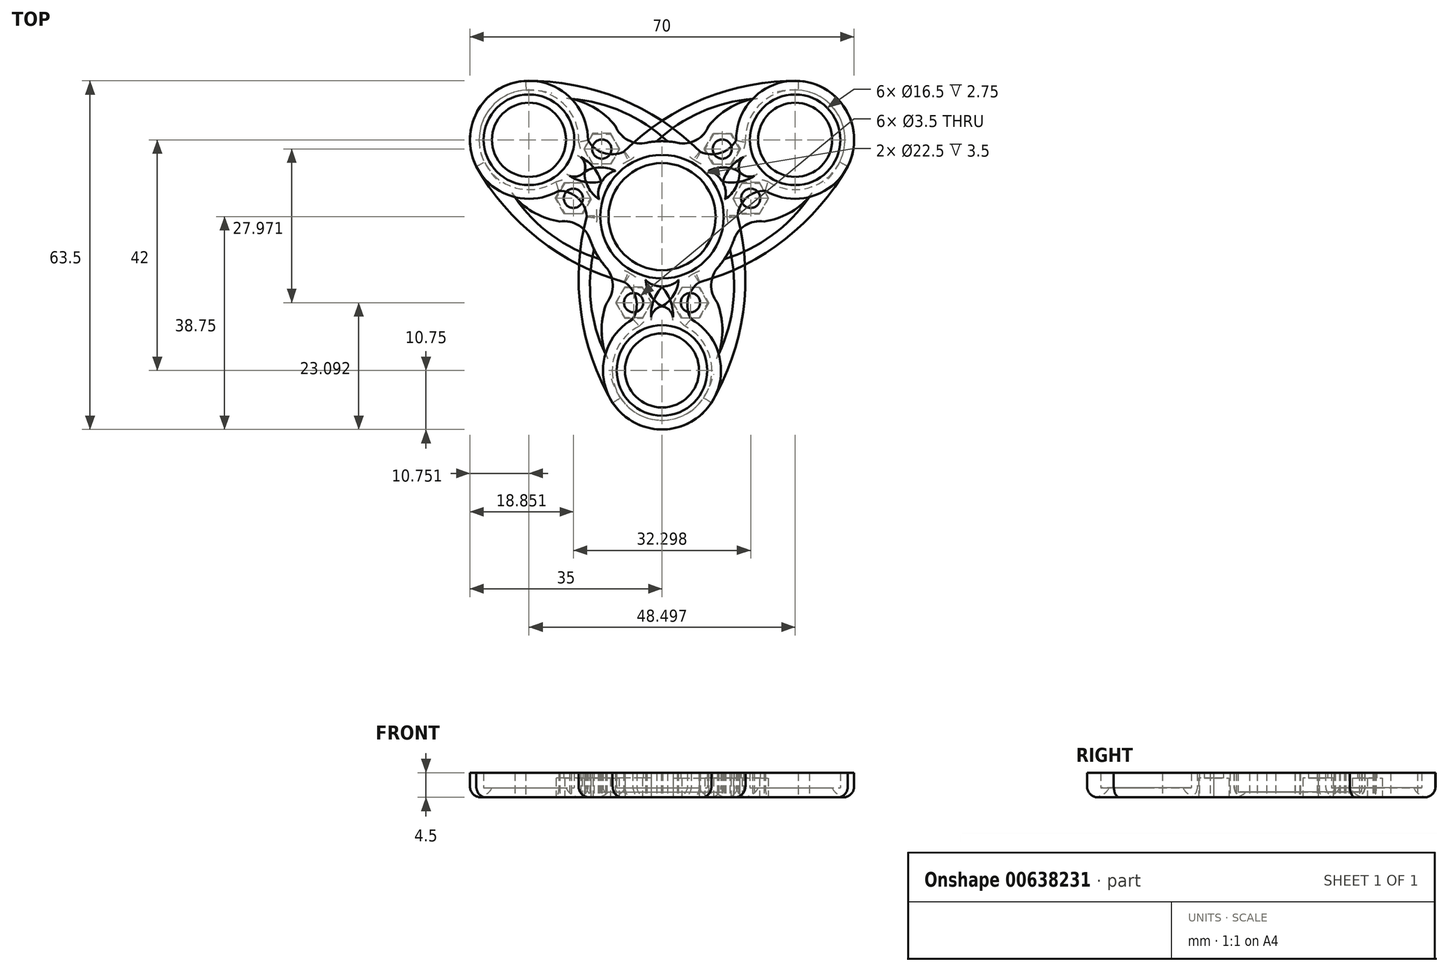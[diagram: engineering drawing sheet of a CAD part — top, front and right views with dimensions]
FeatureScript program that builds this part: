
annotation { "Feature Type Name" : "Feature", "Feature Type Description" : "" }
export const myFeature = defineFeature(function(context is Context, id is Id, definition is map)
    precondition{}
    {
        {
            assignVariable(context, id + "F0", {"name" : "OuterBearingHeight", "anyValue" : 5});
        }
        {
            assignVariable(context, id + "F1", {"name" : "CenterBearingHeight", "anyValue" : 7});
        }
        {
            var Q0;
            Q0=qCreatedBy(makeId("Top.planeOp"),FACE);
            var sketch = newSketch(context, id + "F2", { "sketchPlane" : qUnion([Q0])});
            skCircle(sketch, "E0", {"center": v(0, 0) * mm, "radius": 11.25 * mm});
            skCircle(sketch, "E1", {"center": v(0, 0) * mm, "radius": 9.75 * mm});
            skCircle(sketch, "E2", {"center": v(0, 0) * mm, "radius": 13.75 * mm});
            skCircle(sketch, "E3", {"center": v(0, -28) * mm, "radius": 10.75 * mm});
            skArc(sketch, "E4", {"start": v(-13.75, 0) * mm, "mid": v(-14.77, -17.41) * mm, "end": v(-9, -33.88) * mm});
            skArc(sketch, "E5", {"start": v(6.75, -11.98) * mm, "mid": v(4.65, -16.78) * mm, "end": v(8, -20.82) * mm});
            skPoint(sketch, "E6.center", {"position": v(0.04, 0.07) * mm});
            skCircle(sketch, "E7.cCircle", {"center": v(-5.18, -15.66) * mm, "radius": 2.75 * mm, "construction": true});
            skLineSegment(sketch, "E7.0", {"start": v(-3.59, -18.4) * mm, "end": v(-6.76, -18.4) * mm});
            skLineSegment(sketch, "E7.1", {"start": v(-6.76, -18.4) * mm, "end": v(-8.35, -15.66) * mm});
            skLineSegment(sketch, "E7.2", {"start": v(-8.35, -15.66) * mm, "end": v(-6.76, -12.9) * mm});
            skLineSegment(sketch, "E7.3", {"start": v(-6.76, -12.9) * mm, "end": v(-3.59, -12.9) * mm});
            skLineSegment(sketch, "E7.4", {"start": v(-3.59, -12.9) * mm, "end": v(-2, -15.66) * mm});
            skLineSegment(sketch, "E7.5", {"start": v(-2, -15.66) * mm, "end": v(-3.59, -18.4) * mm});
            skPoint(sketch, "E7.0.midPoint", {"position": v(-5.18, -18.4) * mm});
            skLineSegment(sketch, "E8", {"start": v(-5.18, -15.66) * mm, "end": v(-5.18, -12.74) * mm, "construction": true});
            skLineSegment(sketch, "E9", {"start": v(-5.18, -15.66) * mm, "end": v(-5.18, -18.58) * mm, "construction": true});
            skLineSegment(sketch, "E10", {"start": v(-5.18, -15.66) * mm, "end": v(-14.98, -15.66) * mm, "construction": true});
            skLineSegment(sketch, "E11", {"start": v(-5.18, -15.66) * mm, "end": v(4.62, -15.66) * mm, "construction": true});
            skCircle(sketch, "E12", {"center": v(-5.18, -15.66) * mm, "radius": 1.75 * mm});
            skArc(sketch, "E13", {"start": v(-12.37, -6) * mm, "mid": v(-12.96, -15.68) * mm, "end": v(-10.33, -25.02) * mm});
            skArc(sketch, "E14", {"start": v(-10.08, -15.66) * mm, "mid": v(-11, -20.32) * mm, "end": v(-10.33, -25.02) * mm});
            skArc(sketch, "E15", {"start": v(-10.08, -15.66) * mm, "mid": v(-8.97, -12.35) * mm, "end": v(-10.29, -9.12) * mm});
            skArc(sketch, "E16", {"start": v(2, -18.27) * mm, "mid": v(0.72, -13.72) * mm, "end": v(-3.01, -10.84) * mm});
            skArc(sketch, "E17", {"start": v(2, -18.27) * mm, "mid": v(1.3, -16.98) * mm, "end": v(0, -16.32) * mm});
            skArc(sketch, "E18", {"start": v(-3.01, -10.84) * mm, "mid": v(-2.27, -14) * mm, "end": v(0, -16.32) * mm});
            skCircle(sketch, "E19", {"center": v(0, -28) * mm, "radius": 8.25 * mm});
            skCircle(sketch, "E20", {"center": v(0, -28) * mm, "radius": 6.75 * mm});
            skArc(sketch, "E21", {"start": v(-3, -11.56) * mm, "mid": v(-1.67, -12.41) * mm, "end": v(-0.12, -12.69) * mm});
            skArc(sketch, "E22.1.0", {"start": v(6.87, -11.9) * mm, "mid": v(22.46, -4.08) * mm, "end": v(33.84, 9.15) * mm});
            skArc(sketch, "E22.1.1", {"start": v(11.38, -7.71) * mm, "mid": v(20.06, -3.39) * mm, "end": v(26.83, 3.56) * mm});
            skArc(sketch, "E22.1.2", {"start": v(18.6, -0.9) * mm, "mid": v(15.18, -1.59) * mm, "end": v(13.04, -4.35) * mm});
            skArc(sketch, "E22.1.3", {"start": v(18.6, -0.9) * mm, "mid": v(23.1, 0.63) * mm, "end": v(26.83, 3.56) * mm});
            skLineSegment(sketch, "E22.1.4", {"start": v(19.32, 3.35) * mm, "end": v(17.74, 0.6) * mm});
            skLineSegment(sketch, "E22.1.5", {"start": v(17.74, 0.6) * mm, "end": v(14.56, 0.6) * mm});
            skLineSegment(sketch, "E22.1.6", {"start": v(14.56, 0.6) * mm, "end": v(12.97, 3.35) * mm});
            skLineSegment(sketch, "E22.1.7", {"start": v(12.97, 3.35) * mm, "end": v(14.56, 6.1) * mm});
            skLineSegment(sketch, "E22.1.8", {"start": v(14.56, 6.1) * mm, "end": v(17.74, 6.1) * mm});
            skLineSegment(sketch, "E22.1.9", {"start": v(17.74, 6.1) * mm, "end": v(19.32, 3.35) * mm});
            skCircle(sketch, "E22.1.10", {"center": v(24.25, 14) * mm, "radius": 10.75 * mm});
            skCircle(sketch, "E22.1.11", {"center": v(24.25, 14) * mm, "radius": 8.25 * mm});
            skCircle(sketch, "E22.1.12", {"center": v(24.25, 14) * mm, "radius": 6.75 * mm});
            skArc(sketch, "E22.1.13", {"start": v(10.9, 2.81) * mm, "mid": v(13.26, 5.03) * mm, "end": v(14.13, 8.16) * mm});
            skArc(sketch, "E22.1.14", {"start": v(14.82, 10.86) * mm, "mid": v(11.52, 7.49) * mm, "end": v(10.9, 2.81) * mm});
            skArc(sketch, "E22.1.15", {"start": v(7, 11.84) * mm, "mid": v(12.2, 12.42) * mm, "end": v(14.03, 17.34) * mm});
            skArc(sketch, "E22.1.16", {"start": v(14.82, 10.86) * mm, "mid": v(14.06, 9.62) * mm, "end": v(14.13, 8.16) * mm});
            skArc(sketch, "E22.1.17", {"start": v(11.5, 3.18) * mm, "mid": v(11.59, 4.76) * mm, "end": v(11.05, 6.24) * mm});
            skCircle(sketch, "E22.1.18", {"center": v(16.15, 3.35) * mm, "radius": 1.75 * mm});
            skArc(sketch, "E22.2.0", {"start": v(6.87, 11.9) * mm, "mid": v(-7.7, 21.5) * mm, "end": v(-24.84, 24.73) * mm});
            skArc(sketch, "E22.2.1", {"start": v(1, 13.71) * mm, "mid": v(-7.1, 19.07) * mm, "end": v(-16.5, 21.45) * mm});
            skArc(sketch, "E22.2.2", {"start": v(-8.52, 16.56) * mm, "mid": v(-6.21, 13.94) * mm, "end": v(-2.75, 13.47) * mm});
            skArc(sketch, "E22.2.3", {"start": v(-8.52, 16.56) * mm, "mid": v(-12.1, 19.7) * mm, "end": v(-16.5, 21.45) * mm});
            skLineSegment(sketch, "E22.2.4", {"start": v(-12.56, 15.06) * mm, "end": v(-9.38, 15.06) * mm});
            skLineSegment(sketch, "E22.2.5", {"start": v(-9.38, 15.06) * mm, "end": v(-7.8, 12.31) * mm});
            skLineSegment(sketch, "E22.2.6", {"start": v(-7.8, 12.31) * mm, "end": v(-9.38, 9.56) * mm});
            skLineSegment(sketch, "E22.2.7", {"start": v(-9.38, 9.56) * mm, "end": v(-12.56, 9.56) * mm});
            skLineSegment(sketch, "E22.2.8", {"start": v(-12.56, 9.56) * mm, "end": v(-14.15, 12.31) * mm});
            skLineSegment(sketch, "E22.2.9", {"start": v(-14.15, 12.31) * mm, "end": v(-12.56, 15.06) * mm});
            skCircle(sketch, "E22.2.10", {"center": v(-24.25, 14) * mm, "radius": 10.75 * mm});
            skCircle(sketch, "E22.2.11", {"center": v(-24.25, 14) * mm, "radius": 8.25 * mm});
            skCircle(sketch, "E22.2.12", {"center": v(-24.25, 14) * mm, "radius": 6.75 * mm});
            skArc(sketch, "E22.2.13", {"start": v(-7.88, 8.03) * mm, "mid": v(-10.99, 8.97) * mm, "end": v(-14.13, 8.16) * mm});
            skArc(sketch, "E22.2.14", {"start": v(-16.82, 7.4) * mm, "mid": v(-12.25, 6.24) * mm, "end": v(-7.88, 8.03) * mm});
            skArc(sketch, "E22.2.15", {"start": v(-13.75, 0.14) * mm, "mid": v(-16.86, 4.36) * mm, "end": v(-22.03, 3.48) * mm});
            skArc(sketch, "E22.2.16", {"start": v(-16.82, 7.4) * mm, "mid": v(-15.36, 7.37) * mm, "end": v(-14.13, 8.16) * mm});
            skArc(sketch, "E22.2.17", {"start": v(-8.5, 8.38) * mm, "mid": v(-9.91, 7.66) * mm, "end": v(-10.93, 6.45) * mm});
            skCircle(sketch, "E22.2.18", {"center": v(-10.97, 12.31) * mm, "radius": 1.75 * mm});
            skSolve(sketch);
        }
        {
            var Q0;
            {var subQ0=sQuery(id+"F2.wireOp",EDGE,"E22.2.15");var subQ1=sQuery(id+"F2.wireOp",EDGE,"E2");var subQ2=makeQuery(id+"F2.imprint","INTERSECT",VERTEX,{"derivedFrom":[subQ1,subQ0]});Q0=makeQuery(id+"F2.imprint","IMPRINT",FACE,{"disambiguationData":[TD([[makeQuery(id+"F2.imprint","IMPRINT",EDGE,{"disambiguationData":[TD([[subQ2,1.0]])],"derivedFrom":subQ1}),-1.0]])]});}
            var Q1;
            {var subQ5=sQuery(id+"F2.wireOp",EDGE,"E22.2.7");var subQ7=sQuery(id+"F2.wireOp",EDGE,"E2");var subQ8=makeQuery(id+"F2.imprint","INTERSECT",VERTEX,{"derivedFrom":[subQ7,subQ5]});Q1=makeQuery(id+"F2.imprint","IMPRINT",FACE,{"disambiguationData":[TD([[makeQuery(id+"F2.imprint","IMPRINT",EDGE,{"disambiguationData":[TD([[subQ8,-1.0]])],"derivedFrom":subQ7}),-1.0]])]});}
            var Q2;
            {var subQ1=sQuery(id+"F2.wireOp",EDGE,"E22.2.3");Q2=makeQuery(id+"F2.imprint","IMPRINT",FACE,{"disambiguationData":[TD([[makeQuery(id+"F2.imprint","IMPRINT",EDGE,{"derivedFrom":subQ1}),1.0]])]});}
            var Q3;
            {var subQ3=sQuery(id+"F2.wireOp",EDGE,"E22.2.1");Q3=makeQuery(id+"F2.imprint","IMPRINT",FACE,{"disambiguationData":[TD([[makeQuery(id+"F2.imprint","IMPRINT",EDGE,{"derivedFrom":subQ3}),-1.0]])]});}
            var Q4;
            {var subQ3=sQuery(id+"F2.wireOp",EDGE,"E13");Q4=makeQuery(id+"F2.imprint","IMPRINT",FACE,{"disambiguationData":[TD([[makeQuery(id+"F2.imprint","IMPRINT",EDGE,{"derivedFrom":subQ3}),-1.0]])]});}
            var Q5;
            {var subQ0=sQuery(id+"F2.wireOp",EDGE,"E7.1");Q5=makeQuery(id+"F2.imprint","IMPRINT",FACE,{"disambiguationData":[TD([[makeQuery(id+"F2.imprint","IMPRINT",EDGE,{"derivedFrom":subQ0}),1.0]])]});}
            var Q6;
            {var subQ1=sQuery(id+"F2.wireOp",EDGE,"E7.4");var subQ5=sQuery(id+"F2.wireOp",EDGE,"E2");var subQ6=makeQuery(id+"F2.imprint","INTERSECT",VERTEX,{"derivedFrom":[subQ5,subQ1]});Q6=makeQuery(id+"F2.imprint","IMPRINT",FACE,{"disambiguationData":[TD([[makeQuery(id+"F2.imprint","IMPRINT",EDGE,{"disambiguationData":[TD([[subQ6,-1.0]])],"derivedFrom":subQ5}),-1.0]])]});}
            var Q7;
            {var subQ0=sQuery(id+"F2.wireOp",EDGE,"E5");var subQ1=sQuery(id+"F2.wireOp",EDGE,"E2");var subQ2=makeQuery(id+"F2.imprint","INTERSECT",VERTEX,{"derivedFrom":[subQ1,subQ0]});Q7=makeQuery(id+"F2.imprint","IMPRINT",FACE,{"disambiguationData":[TD([[makeQuery(id+"F2.imprint","IMPRINT",EDGE,{"disambiguationData":[TD([[subQ2,1.0]])],"derivedFrom":subQ1}),-1.0]])]});}
            var Q8;
            {var subQ3=sQuery(id+"F2.wireOp",EDGE,"E22.1.1");Q8=makeQuery(id+"F2.imprint","IMPRINT",FACE,{"disambiguationData":[TD([[makeQuery(id+"F2.imprint","IMPRINT",EDGE,{"derivedFrom":subQ3}),-1.0]])]});}
            var Q9;
            {var subQ1=sQuery(id+"F2.wireOp",EDGE,"E22.1.3");Q9=makeQuery(id+"F2.imprint","IMPRINT",FACE,{"disambiguationData":[TD([[makeQuery(id+"F2.imprint","IMPRINT",EDGE,{"derivedFrom":subQ1}),1.0]])]});}
            var Q10;
            {var subQ5=sQuery(id+"F2.wireOp",EDGE,"E22.1.7");var subQ7=sQuery(id+"F2.wireOp",EDGE,"E2");var subQ8=makeQuery(id+"F2.imprint","INTERSECT",VERTEX,{"derivedFrom":[subQ7,subQ5]});Q10=makeQuery(id+"F2.imprint","IMPRINT",FACE,{"disambiguationData":[TD([[makeQuery(id+"F2.imprint","IMPRINT",EDGE,{"disambiguationData":[TD([[subQ8,-1.0]])],"derivedFrom":subQ7}),-1.0]])]});}
            var Q11;
            {var subQ0=sQuery(id+"F2.wireOp",EDGE,"E22.1.15");var subQ1=sQuery(id+"F2.wireOp",EDGE,"E2");var subQ2=makeQuery(id+"F2.imprint","INTERSECT",VERTEX,{"derivedFrom":[subQ1,subQ0]});Q11=makeQuery(id+"F2.imprint","IMPRINT",FACE,{"disambiguationData":[TD([[makeQuery(id+"F2.imprint","IMPRINT",EDGE,{"disambiguationData":[TD([[subQ2,1.0]])],"derivedFrom":subQ1}),-1.0]])]});}
            var Q12;
            Q12=makeQuery(id+"F2.imprint","IMPRINT",FACE,{"disambiguationData":[TD([[makeQuery(id+"F2.imprint","IMPRINT",EDGE,{"derivedFrom":sQuery(id+"F2.wireOp",EDGE,"E22.2.11")}),-1.0]])]});
            var Q13;
            Q13=makeQuery(id+"F2.imprint","IMPRINT",FACE,{"disambiguationData":[TD([[makeQuery(id+"F2.imprint","IMPRINT",EDGE,{"derivedFrom":sQuery(id+"F2.wireOp",EDGE,"E22.1.11")}),-1.0]])]});
            var Q14;
            Q14=makeQuery(id+"F2.imprint","IMPRINT",FACE,{"disambiguationData":[TD([[makeQuery(id+"F2.imprint","IMPRINT",EDGE,{"derivedFrom":sQuery(id+"F2.wireOp",EDGE,"E19")}),-1.0]])]});
            var Q15;
            {var subQ0=sQuery(id+"F2.wireOp",EDGE,"E5");var subQ1=sQuery(id+"F2.wireOp",EDGE,"E3");var subQ2=makeQuery(id+"F2.imprint","INTERSECT",VERTEX,{"disambiguationData":[OD(0.0)],"derivedFrom":[subQ1,subQ0]});Q15=makeQuery(id+"F2.imprint","IMPRINT",FACE,{"disambiguationData":[TD([[makeQuery(id+"F2.imprint","IMPRINT",EDGE,{"disambiguationData":[TD([[subQ2,-1.0]])],"derivedFrom":subQ1}),1.0]])]});}
            var Q16;
            {var subQ0=sQuery(id+"F2.wireOp",EDGE,"E22.1.15");var subQ1=sQuery(id+"F2.wireOp",EDGE,"E22.1.10");var subQ2=makeQuery(id+"F2.imprint","INTERSECT",VERTEX,{"disambiguationData":[OD(0.0)],"derivedFrom":[subQ1,subQ0]});Q16=makeQuery(id+"F2.imprint","IMPRINT",FACE,{"disambiguationData":[TD([[makeQuery(id+"F2.imprint","IMPRINT",EDGE,{"disambiguationData":[TD([[subQ2,-1.0]])],"derivedFrom":subQ1}),1.0]])]});}
            var Q17;
            {var subQ0=sQuery(id+"F2.wireOp",EDGE,"E22.2.15");var subQ1=sQuery(id+"F2.wireOp",EDGE,"E22.2.10");var subQ2=makeQuery(id+"F2.imprint","INTERSECT",VERTEX,{"disambiguationData":[OD(0.0)],"derivedFrom":[subQ1,subQ0]});Q17=makeQuery(id+"F2.imprint","IMPRINT",FACE,{"disambiguationData":[TD([[makeQuery(id+"F2.imprint","IMPRINT",EDGE,{"disambiguationData":[TD([[subQ2,-1.0]])],"derivedFrom":subQ1}),1.0]])]});}
            var Q18;
            {var subQ1=sQuery(id+"F2.wireOp",EDGE,"E2");var subQ17=makeQuery(id+"F2.imprint","INTERSECT",VERTEX,{"derivedFrom":[subQ1,sQuery(id+"F2.wireOp",EDGE,"E22.2.15")]});Q18=makeQuery(id+"F2.imprint","IMPRINT",FACE,{"disambiguationData":[TD([[makeQuery(id+"F2.imprint","IMPRINT",EDGE,{"disambiguationData":[TD([[subQ17,1.0]])],"derivedFrom":subQ1}),1.0]])]});}
            var Q19;
            {var subQ4=sQuery(id+"F2.wireOp",EDGE,"E2");var subQ16=makeQuery(id+"F2.imprint","INTERSECT",VERTEX,{"derivedFrom":[subQ4,sQuery(id+"F2.wireOp",EDGE,"E22.1.15")]});Q19=makeQuery(id+"F2.imprint","IMPRINT",FACE,{"disambiguationData":[TD([[makeQuery(id+"F2.imprint","IMPRINT",EDGE,{"disambiguationData":[TD([[subQ16,1.0]])],"derivedFrom":subQ4}),1.0]])]});}
            var Q20;
            {var subQ1=sQuery(id+"F2.wireOp",EDGE,"E2");var subQ15=sQuery(id+"F2.wireOp",EDGE,"E22.1.7");var subQ16=makeQuery(id+"F2.imprint","INTERSECT",VERTEX,{"derivedFrom":[subQ1,subQ15]});Q20=makeQuery(id+"F2.imprint","IMPRINT",FACE,{"disambiguationData":[TD([[makeQuery(id+"F2.imprint","IMPRINT",EDGE,{"disambiguationData":[TD([[subQ16,-1.0]])],"derivedFrom":subQ1}),1.0]])]});}
            var Q21;
            {var subQ5=sQuery(id+"F2.wireOp",EDGE,"E22.2.17");Q21=makeQuery(id+"F2.imprint","IMPRINT",FACE,{"disambiguationData":[TD([[makeQuery(id+"F2.imprint","IMPRINT",EDGE,{"derivedFrom":subQ5}),1.0]])]});}
            var Q22;
            {var subQ5=sQuery(id+"F2.wireOp",EDGE,"E22.1.17");Q22=makeQuery(id+"F2.imprint","IMPRINT",FACE,{"disambiguationData":[TD([[makeQuery(id+"F2.imprint","IMPRINT",EDGE,{"derivedFrom":subQ5}),1.0]])]});}
            var Q23;
            {var subQ5=sQuery(id+"F2.wireOp",EDGE,"E21");Q23=makeQuery(id+"F2.imprint","IMPRINT",FACE,{"disambiguationData":[TD([[makeQuery(id+"F2.imprint","IMPRINT",EDGE,{"derivedFrom":subQ5}),1.0]])]});}
            extrude(context, id + "F3", {"entities" : qUnion([Q0, Q1, Q2, Q3, Q4, Q5, Q6, Q7, Q8, Q9, Q10, Q11, Q12, Q13, Q14, Q15, Q16, Q17, Q18, Q19, Q20, Q21, Q22, Q23]), "depth" : ((getVariable(context, 'CenterBearingHeight') / 2) + 1) * mm, "offsetDistance" : 25 * mm});
        }
        {
            var Q0;
            Q0=makeQuery(id+"F2.imprint","IMPRINT",FACE,{"disambiguationData":[TD([[makeQuery(id+"F2.imprint","IMPRINT",EDGE,{"derivedFrom":sQuery(id+"F2.wireOp",EDGE,"f691ac80-1c01-42f0-a88e-231e112aa074.2.2")}),1.0]])]});
            var Q1;
            Q1=makeQuery(id+"F2.imprint","IMPRINT",FACE,{"disambiguationData":[TD([[makeQuery(id+"F2.imprint","IMPRINT",EDGE,{"derivedFrom":sQuery(id+"F2.wireOp",EDGE,"f691ac80-1c01-42f0-a88e-231e112aa074.1.2")}),1.0]])]});
            var Q2;
            Q2=makeQuery(id+"F2.imprint","IMPRINT",FACE,{"disambiguationData":[TD([[makeQuery(id+"F2.imprint","IMPRINT",EDGE,{"derivedFrom":sQuery(id+"F2.wireOp",EDGE,"aKZDALUb-4dyq-ynNd-1TMt-uQF9IDW9dU3x")}),1.0]])]});
            var Q3;
            Q3=makeQuery(id+"F2.imprint","IMPRINT",FACE,{"disambiguationData":[TD([[makeQuery(id+"F2.imprint","IMPRINT",EDGE,{"derivedFrom":sQuery(id+"F2.wireOp",EDGE,"E19")}),1.0]])]});
            var Q4;
            Q4=makeQuery(id+"F2.imprint","IMPRINT",FACE,{"disambiguationData":[TD([[makeQuery(id+"F2.imprint","IMPRINT",EDGE,{"derivedFrom":sQuery(id+"F2.wireOp",EDGE,"bf4e577f-11ea-4811-9a98-52c5fba5ef4c.2.13")}),1.0]])]});
            var Q5;
            Q5=makeQuery(id+"F2.imprint","IMPRINT",FACE,{"disambiguationData":[TD([[makeQuery(id+"F2.imprint","IMPRINT",EDGE,{"derivedFrom":sQuery(id+"F2.wireOp",EDGE,"bf4e577f-11ea-4811-9a98-52c5fba5ef4c.1.13")}),1.0]])]});
            var Q6;
            Q6=makeQuery(id+"F2.imprint","IMPRINT",FACE,{"disambiguationData":[TD([[makeQuery(id+"F2.imprint","IMPRINT",EDGE,{"derivedFrom":sQuery(id+"F2.wireOp",EDGE,"E22.1.11")}),1.0]])]});
            var Q7;
            Q7=makeQuery(id+"F2.imprint","IMPRINT",FACE,{"disambiguationData":[TD([[makeQuery(id+"F2.imprint","IMPRINT",EDGE,{"derivedFrom":sQuery(id+"F2.wireOp",EDGE,"E22.2.11")}),1.0]])]});
            extrude(context, id + "F4", {"entities" : qUnion([Q0, Q1, Q2, Q3, Q4, Q5, Q6, Q7]), "operationType" : NewBodyOperationType.ADD, "depth" : (((getVariable(context, 'CenterBearingHeight') / 2) + .75) - getVariable(context, 'OuterBearingHeight') / 2) * mm, "offsetDistance" : 25 * mm});
        }
        {
            var Q0;
            {var subQ3=sQuery(id+"F2.wireOp",EDGE,"E2");var subQ5=sQuery(id+"F2.wireOp",EDGE,"E5");var subQ6=makeQuery(id+"F2.imprint","INTERSECT",VERTEX,{"derivedFrom":[subQ3,subQ5]});Q0=makeQuery(id+"F2.imprint","IMPRINT",FACE,{"disambiguationData":[TD([[makeQuery(id+"F2.imprint","IMPRINT",EDGE,{"disambiguationData":[TD([[subQ6,1.0]])],"derivedFrom":subQ3}),-1.0]])]});}
            var Q1;
            {var subQ0=sQuery(id+"F2.wireOp",EDGE,"E7.1");Q1=makeQuery(id+"F2.imprint","IMPRINT",FACE,{"disambiguationData":[TD([[makeQuery(id+"F2.imprint","IMPRINT",EDGE,{"derivedFrom":subQ0}),-1.0]])]});}
            var Q2;
            {var subQ0=sQuery(id+"F2.wireOp",EDGE,"E7.3");var subQ1=sQuery(id+"F2.wireOp",EDGE,"E2");var subQ2=makeQuery(id+"F2.imprint","INTERSECT",VERTEX,{"derivedFrom":[subQ1,subQ0]});Q2=makeQuery(id+"F2.imprint","IMPRINT",FACE,{"disambiguationData":[TD([[makeQuery(id+"F2.imprint","IMPRINT",EDGE,{"disambiguationData":[TD([[subQ2,-1.0]])],"derivedFrom":subQ1}),1.0]])]});}
            var Q3;
            {var subQ0=sQuery(id+"F2.wireOp",EDGE,"E7.5");var subQ1=sQuery(id+"F2.wireOp",EDGE,"E3");var subQ2=makeQuery(id+"F2.imprint","INTERSECT",VERTEX,{"derivedFrom":[subQ1,subQ0]});Q3=makeQuery(id+"F2.imprint","IMPRINT",FACE,{"disambiguationData":[TD([[makeQuery(id+"F2.imprint","IMPRINT",EDGE,{"disambiguationData":[TD([[subQ2,-1.0]])],"derivedFrom":subQ1}),1.0]])]});}
            var Q4;
            {var subQ1=sQuery(id+"F2.wireOp",EDGE,"bf4e577f-11ea-4811-9a98-52c5fba5ef4c.2.1");Q4=makeQuery(id+"F2.imprint","IMPRINT",FACE,{"disambiguationData":[TD([[makeQuery(id+"F2.imprint","IMPRINT",EDGE,{"derivedFrom":subQ1}),-1.0]])]});}
            var Q5;
            {var subQ0=sQuery(id+"F2.wireOp",EDGE,"bf4e577f-11ea-4811-9a98-52c5fba5ef4c.2.2");var subQ1=sQuery(id+"F2.wireOp",EDGE,"E2");var subQ2=makeQuery(id+"F2.imprint","INTERSECT",VERTEX,{"derivedFrom":[subQ1,subQ0]});Q5=makeQuery(id+"F2.imprint","IMPRINT",FACE,{"disambiguationData":[TD([[makeQuery(id+"F2.imprint","IMPRINT",EDGE,{"disambiguationData":[TD([[subQ2,-1.0]])],"derivedFrom":subQ1}),1.0]])]});}
            var Q6;
            {var subQ0=sQuery(id+"F2.wireOp",EDGE,"bf4e577f-11ea-4811-9a98-52c5fba5ef4c.2.7");var subQ1=sQuery(id+"F2.wireOp",EDGE,"bf4e577f-11ea-4811-9a98-52c5fba5ef4c.2.6");var subQ2=makeQuery(id+"F2.imprint","INTERSECT",VERTEX,{"derivedFrom":[subQ1,subQ0]});Q6=makeQuery(id+"F2.imprint","IMPRINT",FACE,{"disambiguationData":[TD([[makeQuery(id+"F2.imprint","IMPRINT",EDGE,{"disambiguationData":[TD([[subQ2,-1.0]])],"derivedFrom":subQ1}),-1.0]])]});}
            var Q7;
            {var subQ1=sQuery(id+"F2.wireOp",EDGE,"bf4e577f-11ea-4811-9a98-52c5fba5ef4c.1.1");Q7=makeQuery(id+"F2.imprint","IMPRINT",FACE,{"disambiguationData":[TD([[makeQuery(id+"F2.imprint","IMPRINT",EDGE,{"derivedFrom":subQ1}),-1.0]])]});}
            var Q8;
            {var subQ0=sQuery(id+"F2.wireOp",EDGE,"bf4e577f-11ea-4811-9a98-52c5fba5ef4c.1.7");var subQ1=sQuery(id+"F2.wireOp",EDGE,"bf4e577f-11ea-4811-9a98-52c5fba5ef4c.1.6");var subQ2=makeQuery(id+"F2.imprint","INTERSECT",VERTEX,{"derivedFrom":[subQ1,subQ0]});Q8=makeQuery(id+"F2.imprint","IMPRINT",FACE,{"disambiguationData":[TD([[makeQuery(id+"F2.imprint","IMPRINT",EDGE,{"disambiguationData":[TD([[subQ2,-1.0]])],"derivedFrom":subQ1}),-1.0]])]});}
            var Q9;
            {var subQ0=sQuery(id+"F2.wireOp",EDGE,"bf4e577f-11ea-4811-9a98-52c5fba5ef4c.1.8");var subQ1=sQuery(id+"F2.wireOp",EDGE,"E2");var subQ2=makeQuery(id+"F2.imprint","INTERSECT",VERTEX,{"derivedFrom":[subQ1,subQ0]});Q9=makeQuery(id+"F2.imprint","IMPRINT",FACE,{"disambiguationData":[TD([[makeQuery(id+"F2.imprint","IMPRINT",EDGE,{"disambiguationData":[TD([[subQ2,1.0]])],"derivedFrom":subQ1}),1.0]])]});}
            var Q10;
            {var subQ4=sQuery(id+"F2.wireOp",EDGE,"E22.1.4");Q10=makeQuery(id+"F2.imprint","IMPRINT",FACE,{"disambiguationData":[TD([[makeQuery(id+"F2.imprint","IMPRINT",EDGE,{"derivedFrom":subQ4}),-1.0]])]});}
            var Q11;
            {var subQ0=sQuery(id+"F2.wireOp",EDGE,"E22.1.7");var subQ1=sQuery(id+"F2.wireOp",EDGE,"E2");var subQ2=makeQuery(id+"F2.imprint","INTERSECT",VERTEX,{"derivedFrom":[subQ1,subQ0]});Q11=makeQuery(id+"F2.imprint","IMPRINT",FACE,{"disambiguationData":[TD([[makeQuery(id+"F2.imprint","IMPRINT",EDGE,{"disambiguationData":[TD([[subQ2,1.0]])],"derivedFrom":subQ1}),1.0]])]});}
            var Q12;
            {var subQ0=sQuery(id+"F2.wireOp",EDGE,"E22.1.9");var subQ1=sQuery(id+"F2.wireOp",EDGE,"E22.1.8");var subQ2=makeQuery(id+"F2.imprint","INTERSECT",VERTEX,{"derivedFrom":[subQ1,subQ0]});Q12=makeQuery(id+"F2.imprint","IMPRINT",FACE,{"disambiguationData":[TD([[makeQuery(id+"F2.imprint","IMPRINT",EDGE,{"disambiguationData":[TD([[subQ2,1.0]])],"derivedFrom":subQ1}),-1.0]])]});}
            var Q13;
            {var subQ4=sQuery(id+"F2.wireOp",EDGE,"E22.2.4");Q13=makeQuery(id+"F2.imprint","IMPRINT",FACE,{"disambiguationData":[TD([[makeQuery(id+"F2.imprint","IMPRINT",EDGE,{"derivedFrom":subQ4}),-1.0]])]});}
            var Q14;
            {var subQ0=sQuery(id+"F2.wireOp",EDGE,"E22.2.6");var subQ1=sQuery(id+"F2.wireOp",EDGE,"E2");var subQ2=makeQuery(id+"F2.imprint","INTERSECT",VERTEX,{"derivedFrom":[subQ1,subQ0]});Q14=makeQuery(id+"F2.imprint","IMPRINT",FACE,{"disambiguationData":[TD([[makeQuery(id+"F2.imprint","IMPRINT",EDGE,{"disambiguationData":[TD([[subQ2,-1.0]])],"derivedFrom":subQ1}),1.0]])]});}
            var Q15;
            {var subQ0=sQuery(id+"F2.wireOp",EDGE,"E22.2.9");var subQ1=sQuery(id+"F2.wireOp",EDGE,"E22.2.8");var subQ2=makeQuery(id+"F2.imprint","INTERSECT",VERTEX,{"derivedFrom":[subQ1,subQ0]});Q15=makeQuery(id+"F2.imprint","IMPRINT",FACE,{"disambiguationData":[TD([[makeQuery(id+"F2.imprint","IMPRINT",EDGE,{"disambiguationData":[TD([[subQ2,1.0]])],"derivedFrom":subQ1}),-1.0]])]});}
            extrude(context, id + "F5", {"entities" : qUnion([Q0, Q1, Q2, Q3, Q4, Q5, Q6, Q7, Q8, Q9, Q10, Q11, Q12, Q13, Q14, Q15]), "operationType" : NewBodyOperationType.ADD, "depth" : ((getVariable(context, 'CenterBearingHeight') / 2) + 1) * mm, "offsetDistance" : 25 * mm, "hasSecondDirection" : true, "secondDirectionOppositeDirection" : false, "secondDirectionDepth" : 3.5 * mm});
        }
        {
            var Q0;
            Q0=makeQuery(id+"F2.imprint","IMPRINT",FACE,{"disambiguationData":[TD([[makeQuery(id+"F2.imprint","IMPRINT",EDGE,{"derivedFrom":sQuery(id+"F2.wireOp",EDGE,"E0")}),1.0]])]});
            var Q1;
            {var subQ0=sQuery(id+"F2.wireOp",EDGE,"E16");var subQ1=sQuery(id+"F2.wireOp",EDGE,"E0");var subQ3=makeQuery(id+"F2.imprint","INTERSECT",VERTEX,{"derivedFrom":[subQ1,subQ0]});Q1=makeQuery(id+"F2.imprint","IMPRINT",FACE,{"disambiguationData":[TD([[makeQuery(id+"F2.imprint","IMPRINT",EDGE,{"disambiguationData":[TD([[subQ3,1.0]])],"derivedFrom":subQ1}),1.0]])]});}
            extrude(context, id + "F6", {"entities" : qUnion([Q0, Q1]), "operationType" : NewBodyOperationType.ADD, "depth" : 1 * mm, "offsetDistance" : 25 * mm});
        }
        {
            var Q0;
            Q0=makeQuery(id+"F3.opExtrude","CAP_EDGE",EDGE,{"disambiguationData":[OSD([sQuery(id+"F2.wireOp",EDGE,"E4")])],"isStart":true});
            var Q1;
            Q1=makeQuery(id+"F3.opExtrude","CAP_EDGE",EDGE,{"disambiguationData":[OSD([sQuery(id+"F2.wireOp",EDGE,"E22.2.15")])],"isStart":true});
            var Q2;
            Q2=makeQuery(id+"F3.opExtrude","CAP_EDGE",EDGE,{"disambiguationData":[OSD([sQuery(id+"F2.wireOp",EDGE,"E3")])],"isStart":true});
            var Q3;
            Q3=makeQuery(id+"F3.opExtrude","CAP_EDGE",EDGE,{"disambiguationData":[OSD([sQuery(id+"F2.wireOp",EDGE,"E22.2.10")])],"isStart":true});
            var Q4;
            Q4=makeQuery(id+"F3.opExtrude","CAP_EDGE",EDGE,{"disambiguationData":[OSD([sQuery(id+"F2.wireOp",EDGE,"E22.2.0")])],"isStart":true});
            var Q5;
            Q5=makeQuery(id+"F3.opExtrude","CAP_EDGE",EDGE,{"disambiguationData":[OSD([sQuery(id+"F2.wireOp",EDGE,"E22.1.15")])],"isStart":true});
            var Q6;
            Q6=makeQuery(id+"F3.opExtrude","CAP_EDGE",EDGE,{"disambiguationData":[OSD([sQuery(id+"F2.wireOp",EDGE,"E22.1.10")])],"isStart":true});
            var Q7;
            Q7=makeQuery(id+"F3.opExtrude","CAP_EDGE",EDGE,{"disambiguationData":[OSD([sQuery(id+"F2.wireOp",EDGE,"E22.1.0")])],"isStart":true});
            var Q8;
            Q8=makeQuery(id+"F3.opExtrude","CAP_EDGE",EDGE,{"disambiguationData":[OSD([sQuery(id+"F2.wireOp",EDGE,"E5")])],"isStart":true});
            var Q9;
            {var subQ0=sQuery(id+"F2.wireOp",EDGE,"E2");Q9=makeQuery(id+"F3.opExtrude","CAP_EDGE",EDGE,{"disambiguationData":[OSD([subQ0]),TDD([makeQuery(id+"F2.imprint","IMPRINT",EDGE,{"disambiguationData":[TD([[makeQuery(id+"F2.imprint","INTERSECT",VERTEX,{"derivedFrom":[subQ0,sQuery(id+"F2.wireOp",EDGE,"E5")]}),-1.0]])],"derivedFrom":subQ0})])],"isStart":true});}
            var Q10;
            {var subQ0=sQuery(id+"F2.wireOp",EDGE,"E2");Q10=makeQuery(id+"F3.opExtrude","CAP_EDGE",EDGE,{"disambiguationData":[OSD([subQ0]),TDD([makeQuery(id+"F2.imprint","IMPRINT",EDGE,{"disambiguationData":[TD([[makeQuery(id+"F2.imprint","INTERSECT",VERTEX,{"derivedFrom":[subQ0,sQuery(id+"F2.wireOp",EDGE,"E4")]}),1.0]])],"derivedFrom":subQ0})])],"isStart":true});}
            var Q11;
            {var subQ0=sQuery(id+"F2.wireOp",EDGE,"E2");Q11=makeQuery(id+"F3.opExtrude","CAP_EDGE",EDGE,{"disambiguationData":[OSD([subQ0]),TDD([makeQuery(id+"F2.imprint","IMPRINT",EDGE,{"disambiguationData":[TD([[makeQuery(id+"F2.imprint","INTERSECT",VERTEX,{"derivedFrom":[subQ0,sQuery(id+"F2.wireOp",EDGE,"E22.1.15")]}),-1.0]])],"derivedFrom":subQ0})])],"isStart":true});}
            fillet(context, id + "F7", {"entities" : qUnion([Q0, Q1, Q2, Q3, Q4, Q5, Q6, Q7, Q8, Q9, Q10, Q11]), "radius" : 2 * mm, "tangentPropagation" : true, "allowEdgeOverflow" : false});
        }
        {
            var Q0;
            Q0=makeQuery(id+"F4.opExtrude","CAP_EDGE",EDGE,{"disambiguationData":[OSD([sQuery(id+"F2.wireOp",EDGE,"f691ac80-1c01-42f0-a88e-231e112aa074.2.3")])],"isStart":true});
            var Q1;
            Q1=makeQuery(id+"F6.opExtrude","CAP_EDGE",EDGE,{"disambiguationData":[OSD([sQuery(id+"F2.wireOp",EDGE,"E1")])],"isStart":true});
            var Q2;
            Q2=makeQuery(id+"F4.opExtrude","CAP_EDGE",EDGE,{"disambiguationData":[OSD([sQuery(id+"F2.wireOp",EDGE,"udslHx3o-LPzl-F921-wRQS-P6q11kkCxCmo")])],"isStart":true});
            var Q3;
            Q3=makeQuery(id+"F4.opExtrude","CAP_EDGE",EDGE,{"disambiguationData":[OSD([sQuery(id+"F2.wireOp",EDGE,"f691ac80-1c01-42f0-a88e-231e112aa074.1.3")])],"isStart":true});
            var Q4;
            Q4=makeQuery(id+"F4.opExtrude","CAP_EDGE",EDGE,{"disambiguationData":[OSD([sQuery(id+"F2.wireOp",EDGE,"E1")])],"isStart":true});
            var Q5;
            Q5=makeQuery(id+"F4.opExtrude","CAP_EDGE",EDGE,{"disambiguationData":[OSD([sQuery(id+"F2.wireOp",EDGE,"bf4e577f-11ea-4811-9a98-52c5fba5ef4c.2.14")])],"isStart":true});
            var Q6;
            Q6=makeQuery(id+"F4.opExtrude","CAP_EDGE",EDGE,{"disambiguationData":[OSD([sQuery(id+"F2.wireOp",EDGE,"E20")])],"isStart":true});
            var Q7;
            Q7=makeQuery(id+"F4.opExtrude","CAP_EDGE",EDGE,{"disambiguationData":[OSD([sQuery(id+"F2.wireOp",EDGE,"bf4e577f-11ea-4811-9a98-52c5fba5ef4c.1.14")])],"isStart":true});
            var Q8;
            Q8=makeQuery(id+"F3.opExtrude","CAP_EDGE",EDGE,{"disambiguationData":[OSD([sQuery(id+"F2.wireOp",EDGE,"E22.2.11")])],"isStart":true});
            var Q9;
            Q9=makeQuery(id+"F3.opExtrude","CAP_EDGE",EDGE,{"disambiguationData":[OSD([sQuery(id+"F2.wireOp",EDGE,"E22.1.11")])],"isStart":true});
            var Q10;
            Q10=makeQuery(id+"F4.opExtrude","CAP_EDGE",EDGE,{"disambiguationData":[OSD([sQuery(id+"F2.wireOp",EDGE,"E22.2.12")])],"isStart":true});
            var Q11;
            Q11=makeQuery(id+"F4.opExtrude","CAP_EDGE",EDGE,{"disambiguationData":[OSD([sQuery(id+"F2.wireOp",EDGE,"E22.1.12")])],"isStart":true});
            fillet(context, id + "F8", {"entities" : qUnion([Q0, Q1, Q2, Q3, Q4, Q5, Q6, Q7, Q8, Q9, Q10, Q11]), "radius" : 3 * mm, "tangentPropagation" : true, "allowEdgeOverflow" : false});
        }
        {
            var Q0;
            Q0=makeQuery(id+"F3.opExtrude","CAP_EDGE",EDGE,{"disambiguationData":[OSD([sQuery(id+"F2.wireOp",EDGE,"E22.2.2")])],"isStart":true});
            var Q1;
            {var subQ0=sQuery(id+"F2.wireOp",EDGE,"E2");Q1=makeQuery(id+"F3.opExtrude","CAP_EDGE",EDGE,{"disambiguationData":[OSD([subQ0]),TDD([makeQuery(id+"F2.imprint","IMPRINT",EDGE,{"disambiguationData":[TD([[makeQuery(id+"F2.imprint","INTERSECT",VERTEX,{"derivedFrom":[subQ0,sQuery(id+"F2.wireOp",EDGE,"E22.2.1")]}),-1.0]])],"derivedFrom":subQ0})])],"isStart":true});}
            var Q2;
            Q2=makeQuery(id+"F7.opFillet","BLEND_EDGE",EDGE,{"blendedFrom":[makeQuery(id+"F3.opExtrude","CAP_EDGE",EDGE,{"disambiguationData":[OSD([sQuery(id+"F2.wireOp",EDGE,"E22.2.0")])],"isStart":true}),makeQuery(id+"F3.opExtrude","SWEPT_FACE",FACE,{"disambiguationData":[OSD([sQuery(id+"F2.wireOp",EDGE,"E22.2.1")])]})],"blendedInto":[makeQuery(id+"F3.opExtrude","SWEPT_FACE",FACE,{"disambiguationData":[OSD([sQuery(id+"F2.wireOp",EDGE,"E22.2.1")])]})]});
            var Q3;
            Q3=makeQuery(id+"F3.opExtrude","CAP_EDGE",EDGE,{"disambiguationData":[OSD([sQuery(id+"F2.wireOp",EDGE,"E22.2.3")])],"isStart":true});
            var Q4;
            {var subQ0=sQuery(id+"F2.wireOp",EDGE,"E2");Q4=makeQuery(id+"F3.opExtrude","CAP_EDGE",EDGE,{"disambiguationData":[OSD([subQ0]),TDD([makeQuery(id+"F2.imprint","IMPRINT",EDGE,{"disambiguationData":[TD([[makeQuery(id+"F2.imprint","INTERSECT",VERTEX,{"derivedFrom":[subQ0,sQuery(id+"F2.wireOp",EDGE,"E22.1.1")]}),-1.0]])],"derivedFrom":subQ0})])],"isStart":true});}
            var Q5;
            Q5=makeQuery(id+"F3.opExtrude","CAP_EDGE",EDGE,{"disambiguationData":[OSD([sQuery(id+"F2.wireOp",EDGE,"E22.1.2")])],"isStart":true});
            var Q6;
            Q6=makeQuery(id+"F3.opExtrude","CAP_EDGE",EDGE,{"disambiguationData":[OSD([sQuery(id+"F2.wireOp",EDGE,"E22.1.3")])],"isStart":true});
            var Q7;
            Q7=makeQuery(id+"F7.opFillet","BLEND_EDGE",EDGE,{"blendedFrom":[makeQuery(id+"F3.opExtrude","CAP_EDGE",EDGE,{"disambiguationData":[OSD([sQuery(id+"F2.wireOp",EDGE,"E22.1.0")])],"isStart":true}),makeQuery(id+"F3.opExtrude","SWEPT_FACE",FACE,{"disambiguationData":[OSD([sQuery(id+"F2.wireOp",EDGE,"E22.1.1")])]})],"blendedInto":[makeQuery(id+"F3.opExtrude","SWEPT_FACE",FACE,{"disambiguationData":[OSD([sQuery(id+"F2.wireOp",EDGE,"E22.1.1")])]})]});
            var Q8;
            Q8=makeQuery(id+"F3.opExtrude","CAP_EDGE",EDGE,{"disambiguationData":[OSD([sQuery(id+"F2.wireOp",EDGE,"E15")])],"isStart":true});
            var Q9;
            Q9=makeQuery(id+"F3.opExtrude","CAP_EDGE",EDGE,{"disambiguationData":[OSD([sQuery(id+"F2.wireOp",EDGE,"E14")])],"isStart":true});
            var Q10;
            Q10=makeQuery(id+"F7.opFillet","BLEND_EDGE",EDGE,{"blendedFrom":[makeQuery(id+"F3.opExtrude","CAP_EDGE",EDGE,{"disambiguationData":[OSD([sQuery(id+"F2.wireOp",EDGE,"E4")])],"isStart":true}),makeQuery(id+"F3.opExtrude","SWEPT_FACE",FACE,{"disambiguationData":[OSD([sQuery(id+"F2.wireOp",EDGE,"E13")])]})],"blendedInto":[makeQuery(id+"F3.opExtrude","SWEPT_FACE",FACE,{"disambiguationData":[OSD([sQuery(id+"F2.wireOp",EDGE,"E13")])]})]});
            var Q11;
            {var subQ0=sQuery(id+"F2.wireOp",EDGE,"E2");Q11=makeQuery(id+"F3.opExtrude","CAP_EDGE",EDGE,{"disambiguationData":[OSD([subQ0]),TDD([makeQuery(id+"F2.imprint","IMPRINT",EDGE,{"disambiguationData":[TD([[makeQuery(id+"F2.imprint","INTERSECT",VERTEX,{"derivedFrom":[subQ0,sQuery(id+"F2.wireOp",EDGE,"E13")]}),-1.0]])],"derivedFrom":subQ0})])],"isStart":true});}
            var Q12;
            Q12=makeQuery(id+"F3.opExtrude","CAP_EDGE",EDGE,{"disambiguationData":[OSD([sQuery(id+"F2.wireOp",EDGE,"E21")])],"isStart":true});
            var Q13;
            Q13=makeQuery(id+"F3.opExtrude","CAP_EDGE",EDGE,{"disambiguationData":[OSD([sQuery(id+"F2.wireOp",EDGE,"E17")])],"isStart":true});
            var Q14;
            Q14=makeQuery(id+"F3.opExtrude","CAP_EDGE",EDGE,{"disambiguationData":[OSD([sQuery(id+"F2.wireOp",EDGE,"E22.2.16")])],"isStart":true});
            var Q15;
            Q15=makeQuery(id+"F3.opExtrude","CAP_EDGE",EDGE,{"disambiguationData":[OSD([sQuery(id+"F2.wireOp",EDGE,"E22.2.17")])],"isStart":true});
            var Q16;
            Q16=makeQuery(id+"F3.opExtrude","CAP_EDGE",EDGE,{"disambiguationData":[OSD([sQuery(id+"F2.wireOp",EDGE,"E22.1.17")])],"isStart":true});
            var Q17;
            Q17=makeQuery(id+"F3.opExtrude","CAP_EDGE",EDGE,{"disambiguationData":[OSD([sQuery(id+"F2.wireOp",EDGE,"E22.1.16")])],"isStart":true});
            var Q18;
            Q18=makeQuery(id+"F3.opExtrude","CAP_EDGE",EDGE,{"disambiguationData":[OSD([sQuery(id+"F2.wireOp",EDGE,"E22.2.8")])],"isStart":true});
            var Q19;
            Q19=makeQuery(id+"F3.opExtrude","CAP_EDGE",EDGE,{"disambiguationData":[OSD([sQuery(id+"F2.wireOp",EDGE,"E22.2.6")])],"isStart":true});
            var Q20;
            Q20=makeQuery(id+"F3.opExtrude","CAP_EDGE",EDGE,{"disambiguationData":[OSD([sQuery(id+"F2.wireOp",EDGE,"E22.2.5")])],"isStart":true});
            var Q21;
            Q21=makeQuery(id+"F3.opExtrude","CAP_EDGE",EDGE,{"disambiguationData":[OSD([sQuery(id+"F2.wireOp",EDGE,"E22.2.4")])],"isStart":true});
            var Q22;
            Q22=makeQuery(id+"F3.opExtrude","CAP_EDGE",EDGE,{"disambiguationData":[OSD([sQuery(id+"F2.wireOp",EDGE,"E22.2.9")])],"isStart":true});
            var Q23;
            Q23=makeQuery(id+"F3.opExtrude","CAP_EDGE",EDGE,{"disambiguationData":[OSD([sQuery(id+"F2.wireOp",EDGE,"E22.1.8")])],"isStart":true});
            var Q24;
            Q24=makeQuery(id+"F3.opExtrude","CAP_EDGE",EDGE,{"disambiguationData":[OSD([sQuery(id+"F2.wireOp",EDGE,"E22.1.6")])],"isStart":true});
            var Q25;
            Q25=makeQuery(id+"F3.opExtrude","CAP_EDGE",EDGE,{"disambiguationData":[OSD([sQuery(id+"F2.wireOp",EDGE,"E22.1.5")])],"isStart":true});
            var Q26;
            Q26=makeQuery(id+"F3.opExtrude","CAP_EDGE",EDGE,{"disambiguationData":[OSD([sQuery(id+"F2.wireOp",EDGE,"E22.1.4")])],"isStart":true});
            var Q27;
            Q27=makeQuery(id+"F3.opExtrude","CAP_EDGE",EDGE,{"disambiguationData":[OSD([sQuery(id+"F2.wireOp",EDGE,"E22.1.9")])],"isStart":true});
            var Q28;
            Q28=makeQuery(id+"F3.opExtrude","CAP_EDGE",EDGE,{"disambiguationData":[OSD([sQuery(id+"F2.wireOp",EDGE,"E7.3")])],"isStart":true});
            var Q29;
            Q29=makeQuery(id+"F3.opExtrude","CAP_EDGE",EDGE,{"disambiguationData":[OSD([sQuery(id+"F2.wireOp",EDGE,"E7.2")])],"isStart":true});
            var Q30;
            Q30=makeQuery(id+"F3.opExtrude","CAP_EDGE",EDGE,{"disambiguationData":[OSD([sQuery(id+"F2.wireOp",EDGE,"E7.1")])],"isStart":true});
            var Q31;
            Q31=makeQuery(id+"F3.opExtrude","CAP_EDGE",EDGE,{"disambiguationData":[OSD([sQuery(id+"F2.wireOp",EDGE,"E7.0")])],"isStart":true});
            var Q32;
            Q32=makeQuery(id+"F3.opExtrude","CAP_EDGE",EDGE,{"disambiguationData":[OSD([sQuery(id+"F2.wireOp",EDGE,"E7.5")])],"isStart":true});
            chamfer(context, id + "F9", {"entities" : qUnion([Q0, Q1, Q2, Q3, Q4, Q5, Q6, Q7, Q8, Q9, Q10, Q11, Q12, Q13, Q14, Q15, Q16, Q17, Q18, Q19, Q20, Q21, Q22, Q23, Q24, Q25, Q26, Q27, Q28, Q29, Q30, Q31, Q32]), "width" : .1 * mm, "tangentPropagation" : true});
        }
        {
            var Q0;
            Q0=makeQuery(id+"F3.opExtrude","SWEPT_BODY",BODY,{"disambiguationData":[OSD([sQuery(id+"F2.wireOp",EDGE,"E0"),sQuery(id+"F2.wireOp",EDGE,"E2"),sQuery(id+"F2.wireOp",EDGE,"E3"),sQuery(id+"F2.wireOp",EDGE,"E4"),sQuery(id+"F2.wireOp",EDGE,"E5"),sQuery(id+"F2.wireOp",EDGE,"E7.0"),sQuery(id+"F2.wireOp",EDGE,"E7.1"),sQuery(id+"F2.wireOp",EDGE,"E7.2"),sQuery(id+"F2.wireOp",EDGE,"E7.3"),sQuery(id+"F2.wireOp",EDGE,"E7.4"),sQuery(id+"F2.wireOp",EDGE,"E7.5"),sQuery(id+"F2.wireOp",EDGE,"E13"),sQuery(id+"F2.wireOp",EDGE,"E14"),sQuery(id+"F2.wireOp",EDGE,"E15"),sQuery(id+"F2.wireOp",EDGE,"E16"),sQuery(id+"F2.wireOp",EDGE,"E17"),sQuery(id+"F2.wireOp",EDGE,"E18"),sQuery(id+"F2.wireOp",EDGE,"E19"),sQuery(id+"F2.wireOp",EDGE,"E21"),sQuery(id+"F2.wireOp",EDGE,"E22.1.0"),sQuery(id+"F2.wireOp",EDGE,"E22.1.1"),sQuery(id+"F2.wireOp",EDGE,"E22.1.2"),sQuery(id+"F2.wireOp",EDGE,"E22.1.3"),sQuery(id+"F2.wireOp",EDGE,"E22.1.4"),sQuery(id+"F2.wireOp",EDGE,"E22.1.5"),sQuery(id+"F2.wireOp",EDGE,"E22.1.6"),sQuery(id+"F2.wireOp",EDGE,"E22.1.7"),sQuery(id+"F2.wireOp",EDGE,"E22.1.8"),sQuery(id+"F2.wireOp",EDGE,"E22.1.9"),sQuery(id+"F2.wireOp",EDGE,"E22.1.10"),sQuery(id+"F2.wireOp",EDGE,"E22.1.11"),sQuery(id+"F2.wireOp",EDGE,"E22.1.13"),sQuery(id+"F2.wireOp",EDGE,"E22.1.14"),sQuery(id+"F2.wireOp",EDGE,"E22.1.15"),sQuery(id+"F2.wireOp",EDGE,"E22.1.16"),sQuery(id+"F2.wireOp",EDGE,"E22.1.17"),sQuery(id+"F2.wireOp",EDGE,"E22.2.0"),sQuery(id+"F2.wireOp",EDGE,"E22.2.1"),sQuery(id+"F2.wireOp",EDGE,"E22.2.2"),sQuery(id+"F2.wireOp",EDGE,"E22.2.3"),sQuery(id+"F2.wireOp",EDGE,"E22.2.4"),sQuery(id+"F2.wireOp",EDGE,"E22.2.5"),sQuery(id+"F2.wireOp",EDGE,"E22.2.6"),sQuery(id+"F2.wireOp",EDGE,"E22.2.7"),sQuery(id+"F2.wireOp",EDGE,"E22.2.8"),sQuery(id+"F2.wireOp",EDGE,"E22.2.9"),sQuery(id+"F2.wireOp",EDGE,"E22.2.10"),sQuery(id+"F2.wireOp",EDGE,"E22.2.11"),sQuery(id+"F2.wireOp",EDGE,"E22.2.13"),sQuery(id+"F2.wireOp",EDGE,"E22.2.14"),sQuery(id+"F2.wireOp",EDGE,"E22.2.15"),sQuery(id+"F2.wireOp",EDGE,"E22.2.16"),sQuery(id+"F2.wireOp",EDGE,"E22.2.17")])]});
            var Q1;
            Q1=qCreatedBy(makeId("Right.planeOp"),FACE);
            mirror(context, id + "F10", {"entities" : qUnion([Q0]), "mirrorPlane" : qUnion([Q1])});
        }
    });
